# Revit family: MaviGard Détecteur de Gaz
name_source: partatom
category: Fire Alarm Devices
units: mm (PartAtom-declared; Revit-internal decimal feet)

## family parameters
Cut with Voids When Loaded = No
Host = Face
Maintain Annotation Orientation = Yes
OmniClass Number = 23.85.30.21
OmniClass Title = Environmental Detection/Registration
Part Type = Normal
Room Calculation Point = No
Round Connector Dimension = Use Diameter
Shared = No

## types (13) — shared parameters
Adresse Ligne 1 = Şerifali Mahallesi Kutup Sokak No:27/1-2-4 Ümraniye TR-34775 İSTANBUL
Code de Performance = EN 50194-1
Deuxième Matèriel = Plastique
Durée de la garantie Travail = 2
Durée de la garantie réservé = 2
Hauteur Nominale = 100 mm
Largeur Nominale = 50 mm
Longeur Nominale = 140 mm
Manuel d'Installation = https://mavilielektronik.com
Manufacturer = Mavili Elektronik Ticaret A.Ş.
Model = MaviGard
Numèro de Fax = (+)90 216 466 45 10
Protection de Classe = IP42
Socles Compatible = ML-0120
Tempèrature de Fonctionnement = (-10°C) - (+55°C)
URL = https://www.mavili.com.tr
zero-valued in all types: Cost, Default Elevation

## per-type parameters (varying)
| type | Alimentation d'externe | Charger adresse d'appareil | Code de Produit | Couleur | Description | Hauteur de Montage | Numèro de pose des travaux publics | Principe Matèriel | Surface de Montage | Unité de durée de la garantie | Voltage de fonctionnement (défault) | Voltage fonction d'opération |
| MaviGard Détecteur de Gaz Monoxyde de Carbon 12V  2 sortie niveau d'alarme ,Electrochimique | 24 V/DC |  | GD2R-12EC | Blanc | [CO] Détecteur de Gaz Monoxyde de Carbone | 150 cm | 833-610 | Plastique Blanc PC/ABS | Montage à Mur | Ans | 12 V/DC | 12-33V/DC |
| Mavigard Détecteur de gaz Monoxyde de Carbone 24V  Sortie de 2 niveau d'alarme,Electrochimique | 24 V/DC |  | GD2R-24EC | Blanc | [CO] Détecteur de Monoxyde Carbone | 150 cm | 833-610 | Plastique Blanc PC/ABS | Montage à Mur | Ans | 24 V/DC | 18-33V/DC |
| MaviGard Détecteur de Gaz Monoxyde de Carbon 220V AC 2 Sortie de  niveau,Electrochimique | 220 V/AC |  | GD2R-220EC | Blanc | [CO] Détecteur de Gaz Monoxyde de Carbone | 150 cm | 833-610 | Plastique Blanc PC/ABS | Montage à Mur | Ans | 24 V/DC | 18-33V/DC |
| MaviGard détecteur de Gaz à la série de GDR détecteur de GPL ,12/24V DC,Sortie de Relais | 24 V/DC |  | GDR-1224L | Blanc | LPG gaz dedektörü Détecteur de Gaz ,Gaz Naturel | 15-25 cm | 833-606 | Plastique Blanc PC/ABS | Montage à Mur | Ans | 24 V/DC | 18-33V/DC |
| Mavigard détecteur de Gaz à la série de GDR détecteur de GPL,220V AC,Sortie de Relais | 220 V/DC |  | GDR-220L | Blanc | LPG gaz dedektörü Détecteur de Gaz Naturel Gaz | 15-25 cm | 833-606 | Plastique Blanc PC/ABS | Montage à Mur | Ans | 24 V/DC | 18-33V/DC |
| MaviGard détecteur de gaz à la série de GDR détecteur de Méthane,12/24V DC,Sortie de Relais | 24 V/DC |  | GDR-1224M | Blanc | Metan gaz dedektörü Détecteur de Méthane | Bas de  5-15 cm  Plafonds | 833-608 | Plastique Blanc PC/ABS | Montage à Mur | Ans | 24 V/DC | 12-33V/DC |
| MaviGard Détecteur de Gaz à la série de GDR Détecteur de Méthane ,220V AC,Sortie de Relais | 220 V/AC |  | GDR-220M | Blanc | Détecteur de Gaz Méthane | Bas 5-15 cm de Plafond | 833-608 | Plastique Blanc PC/ABS | Montage à Mur | Ans | 24 V/DC | 18-33V/DC |
| MaviGard Détecteur de Gaz  adressable a la série de AGD ,détecteur de Monoxyde de Carbon,12/24V DC | 24 V/DC | Appareil d'adressage à main | AGD-1224EC.VIP | Blanc | Détecteur de gaz Monoxyde de Carbone Adressable | 150 cm |  | Plastique Blanc PC/ABS | Montage au Mur | Ans | 24 V/DC | 12-33V/DC |
| MaviGard  détecteur de gaz à la série de AGD adressable  détecteur de Monoxyde de Carbon,220V AC | 220 V/AC | Appareil d'adressage à main | AGD-220EC.VIP | Blanc | Détecteur de Monoxyde de Carbone  Adressable | 150 cm |  | Plastique Blanc PC/ABS | Montage à mur | Ans | 24 V/DC | 12-33V/DC |
| MaviGard détecteur de gaz adressable à la série  détecteur de Naturel Gaz 12/24V DC | 24 V/DC | Appareil d'adressage à main | AGD-1224L.VIP | Beyaz | Détecteur de Gaz Naturel Gaz Adressable | 15-25 cm | 833-605 | Plastique Blanc  PC/ABS | Montage à Mur | Year | 24 V/DC | 12-33V/DC |
| MaviGard détecteur de Gaz adressable à la série de AGD détecteur de Naturel Gaz,220V AC | 220 V/AC | Appareil d'adressage à main | AGD-220L.VIP | Beyaz | Détecteur de Gaz Naturel Gaz Adressable | 15-25 cm |  | Plastique Blanc PC/ABS | Montage à Mur | Year | 24 V/DC | 12-33V/DC |
| MaviGard détecteur de gaz  adressable à la série de détecteur de Méthane,12/24V DC | 24 V/DC | Appareil d'adressage à main | AGD-1224M.VIP | Blanc | Détecteur de Gaz Méthane Adressable | 5-15 cm En bas de  plafonds | 833-607 | Plastique Blanc PC/ABS | Montage à Mur | Ans | 24 V/DC | 12-33V/DC |
| MaviGard détecteur à la série de AGD détecteur de Méthane,220V AC | 220 V/AC | Appareil d'adressage à main | AGD-220M.VIP | Blanc | Détecteur de Gaz Méthane Adressable | Bas de  5-15 cm  de Plafonds |  | Plastique Blanc PC/ABS | Montage à Mur | Year | 24 V/DC | 12-33V/DC |

## geometry (parser evidence)
native form markers: Sweep x1
no freeform markers — native parametric forms only
